# Revit family: BC_Hitachi_Yutaki-M-S2_LOD400
name_source: partatom
category: Equipement de génie climatique
revit_build: Autodesk Revit 2018 (Build: 20170223_1515(x64)
units: mm (PartAtom-declared; Revit-internal decimal feet)

## family parameters
Basée sur le plan de construction = Non
Cote de connecteur circulaire = Utiliser le diamètre
Couper avec des vides une fois chargée = Non
Numéro OmniClass = 23.75.70.17
Partagée = Non
Point de calcul de pièce = Non
Titre OmniClass = Water Heated and Cooled Terminal Heating and Cooling Units
Toujours verticalement = Oui
Type d'élément = Normal

## types (2) — shared parameters
BC_OBJECT_ID = 407068
BC_OBJECT_VERSION = #2
Commentaires du type = Yutaki M 2HP (R32)
Description = YUTAKI M R32 (RASM-(2/3)VR2E)
Expansion vessel - internal water volume = 0.01 m³
Fabricant = Hitachi Air Conditioning Europe SAS
Frequency = 50 Hz
Heat Pump Type = ATW Monobloc
Installation Instructions = PMML0647
Manufacturer = Hitachi Air Conditioning Europe SAS
MasterFormat = Split-System Air-Conditioners
Masterformat Code = 23 81 26
Material = White Metal
Minimum installation water volume = 0.03 m³
Modèle = Yutaki M - Series 2
Name BIM&CO = Outdoor Unit
Nominal Static Pressure = 0.0 Pa
Nominal Voltage = 230 V
Nominal energy efficiency 35°C (ηS) = 1.75
Nominal energy efficiency 55°C (ηS) = 1.25
Number of Poles = 1
OmniClass code = 23-33 39 11
Omniclass = Air Conditioners
Outlet water temperature (Cooling) = 5~22
Outlet water temperature (Heating) = 20~60
Overall Depth = 305 mm  [stored 1.00066 ft]
Overall Height = 628 mm  [stored 2.06037 ft]
Overall Width = 1264 mm
SCOP 35°C (Average conditions) = 4.44
Service Space Material = Service Space
Standby power (PSB)  (Average climate) = 0 kW
Support Material = Support
Thermal Power = 0 kW
Uniformat = Distribution Systems
Uniformat code = D3040
Working range (cooling) = 10~46
Working range (heating) = -20~25
zero-valued in all types: Energy efficiency ratio (EER)

## per-type parameters (varying)
- RASM-2VR2E: AC Current Max=13 A; AC Max Power=2.3 kW; AC Nominal Power=0.9 kW; Absorbed power at nominal conditions=1.3 kW; Annual energy consumption (QHE) 35°C application=1862 kWh; Annual energy consumption (QHE) 55°C application=2563 kWh; BC_VARIANT_ID=919392; Breaker Size=16 A; COP (A7/W35)=5; Capacity=4.3 kW; Cooling Capacity Rated=4 kW; Current Rating=4 A; EER (A35/W18)=5.16; EER (A35/W7)=3.82; Hot water flow=0.2 L/s; Mass=83.00 kg; Maximum Air Flow=765.0 L/s; Maximum Current=13 A; Maximum cooling capacity (A35/W18)=7 kW; Maximum cooling capacity (A35/W7)=5.1 kW; Maximum heating capacity (A-7/W35)=5.5 kW; Maximum heating capacity (A-7/W55)=4.8 kW; Nominal Heating Capacity=4300 W; Nominal Water Flow=0.2 L/s; Nominal cooling capacity (A35/W18)=5.5 kW; Nominal cooling capacity (A35/W7)=4 kW; Nominal heating capacity (A7/W35)=4.3 kW; SCOP 55°C (Average conditions)=3.19; SEER (+18°C / +23°C)=8.04; Sound power max=61
- RASM-3VR2E: AC Current Max=17 A; AC Max Power=3.1 kW; AC Nominal Power=1.6 kW; Absorbed power at nominal conditions=2.3 kW; Annual energy consumption (QHE) 35°C application=3101 kWh; Annual energy consumption (QHE) 55°C application=3718 kWh; BC_VARIANT_ID=919393; Breaker Size=20 A; COP (A7/W35)=4.6; Capacity=8 kW; Cooling Capacity Rated=6.5 kW; Current Rating=8 A; EER (A35/W18)=5; EER (A35/W7)=3.35; Hot water flow=0.4 L/s; Mass=85.00 kg; Maximum Air Flow=950.0 L/s; Maximum Current=17 A; Maximum cooling capacity (A35/W18)=9 kW; Maximum cooling capacity (A35/W7)=7 kW; Maximum heating capacity (A-7/W35)=7.5 kW; Maximum heating capacity (A-7/W55)=5.5 kW; Nominal Heating Capacity=8000 W; Nominal Water Flow=0.4 L/s; Nominal cooling capacity (A35/W18)=7 kW; Nominal cooling capacity (A35/W7)=6.5 kW; Nominal heating capacity (A7/W35)=8 kW; SCOP 55°C (Average conditions)=3.2; SEER (+18°C / +23°C)=8.35; Sound power max=66

note: column(s) folded — value = type name in every type: Product Code

note: [stored X ft] marks values corroborated as IEEE doubles in the binary element streams (Revit-internal decimal feet)
